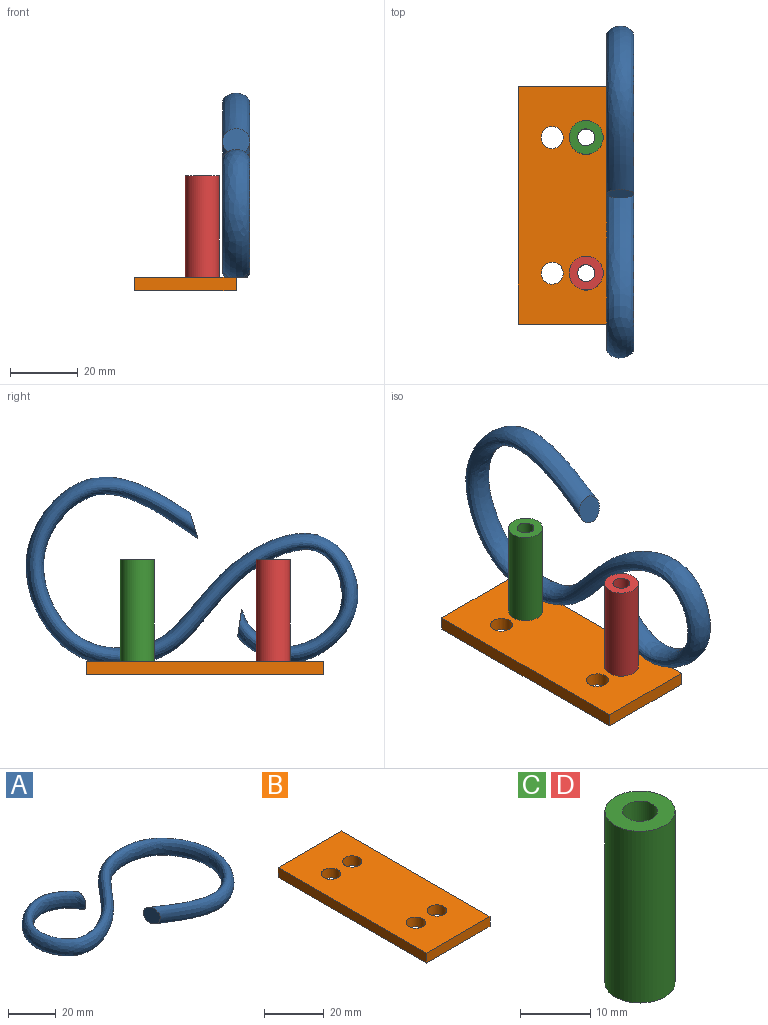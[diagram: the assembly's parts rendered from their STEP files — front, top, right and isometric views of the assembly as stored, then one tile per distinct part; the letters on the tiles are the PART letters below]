
ASSEMBLY  parts=4 mates=3
PART A: 5 faces, bbox 104.3x62x8 mm
  f0: plane 8x7.64mm, normal (-0.95,-0.3,0), area 50.3mm2, adj f2
  f1: plane 8x7.92mm, normal (0.99,-0.14,0), area 50.3mm2, adj f2
  f2: bspline ~104.31x61.95mm, area 4840.1mm2, adj f0,f1,f3,f4
  f3: plane 7.28x4.13mm, normal (0,1,0), area 23.7mm2, adj f2
  f4: plane 17.6x6.64mm, normal (0,1,0), area 95mm2, adj f2
PART B: 10 faces, bbox 30x70x4 mm
  f0: plane 70x4mm, normal (1,0,0), area 280mm2, adj f1,f6,f8,f9
  f1: plane 30x4mm, normal (0,1,0), area 120mm2, adj f0,f2,f8,f9
  f2: plane 70x4mm, normal (-1,0,0), area 280mm2, adj f1,f6,f8,f9
  f3: cylinder r=3.25mm len=6.5mm, axis (0,0,-1), area 81.7mm2, adj f8,f9
  f4: cylinder r=3.25mm len=6.5mm, axis (0,0,-1), area 81.7mm2, adj f8,f9
  f5: cylinder r=3.25mm len=6.5mm, axis (0,0,-1), area 81.7mm2, adj f8,f9
  f6: plane 30x4mm, normal (0,-1,0), area 120mm2, adj f0,f2,f8,f9
  f7: cylinder r=3.25mm len=6.5mm, axis (0,0,-1), area 81.7mm2, adj f8,f9
  f8: plane 70x30mm, normal (0,0,1), area 1967.3mm2, adj f0,f1,f2,f3,f4,f5,f6,f7
  f9: plane 70x30mm, normal (0,0,-1), area 1967.3mm2, adj f0,f1,f2,f3,f4,f5,f6,f7
PART C: 4 faces, bbox 10x10x30 mm
  f0: cylinder r=5mm len=30mm, axis (0,0,-1), area 942.5mm2, adj f1,f2
  f1: plane 10x10mm, normal (0,0,1), area 58.9mm2, adj f0,f3
  f2: plane 10x10mm, normal (0,0,-1), area 58.9mm2, adj f0,f3
  f3: cylinder r=2.5mm len=30mm, axis (0,0,1), area 471.2mm2, adj f1,f2
PART D: same geometry as C
PLACE A rot(axis=(-0.58,-0.58,0.58),120deg) t=(-20.11,42.6,2.52)mm
PLACE B t=(-35.11,17.81,-28.39)mm fixed
PLACE C t=(-30.11,37.81,-24.39)mm
PLACE D t=(-30.11,-2.19,-24.39)mm
MATE fastened A.f4 <-> B.f8  axis (0,0,-1) through (-20.11,42.81,-24.39)mm
MATE fastened C.f0 <-> B.f5  axis (0,0,-1) through (-30.11,37.81,-24.39)mm
MATE fastened D.f0 <-> B.f4  axis (0,0,-1) through (-30.11,-2.19,-24.39)mm
